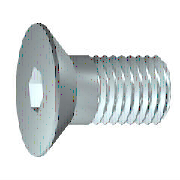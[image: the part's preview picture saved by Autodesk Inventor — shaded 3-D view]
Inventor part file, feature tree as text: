
AUTODESK INVENTOR PART (.ipt)
format: ipt  version: 2024.2 (Build 282272000, 272)  size: 196,096 bytes
history: native  units: mm (DEFAULTED — no unit token found)
features: other x4, sketch x1, fillet x1, chamfer x1
ambient origin geometry x8: Origin, YZ Plane, XZ Plane, XY Plane, X Axis, Y Axis, Z Axis, Center Point
bodies: Solid1 (feature_tree)
feature tree (7):
  sketch  "Sketch1"  dims[d2=3.0mm d3=3.0mm d4=1.5mm d5=1.5mm d6=8.0mm d7=6.0mm d8=360.0deg d9=0.0mm d10=2.0mm d11=2.0mm d12=120.0deg d13=120.0deg d14=120.0deg d15=120.0deg d16=1.2mm d17=0.0mm d18=0.1mm d19=0.25mm d20=45.0deg d22=0.0mm d23=0.0mm d35=0.0mm d37=0.0mm d38=0.0mm d39=0.25mm d40=0.0mm d41=0.0mm d42=0.0mm d43=45.0deg]
  other  "WorkPoint1"
  fillet  "Fillet1"  [1 undecoded]
  chamfer  "Chamfer1"  Distance=3.0mm
  other  "MSC_A1"
  other  "MSC_PF1"
  other  "MSC_PT1"
note: 1 required parameter value undecoded (feature->parameter linkage not recoverable at this tier; creation-order binding heuristic only, values carry confidence <= 0.55)
